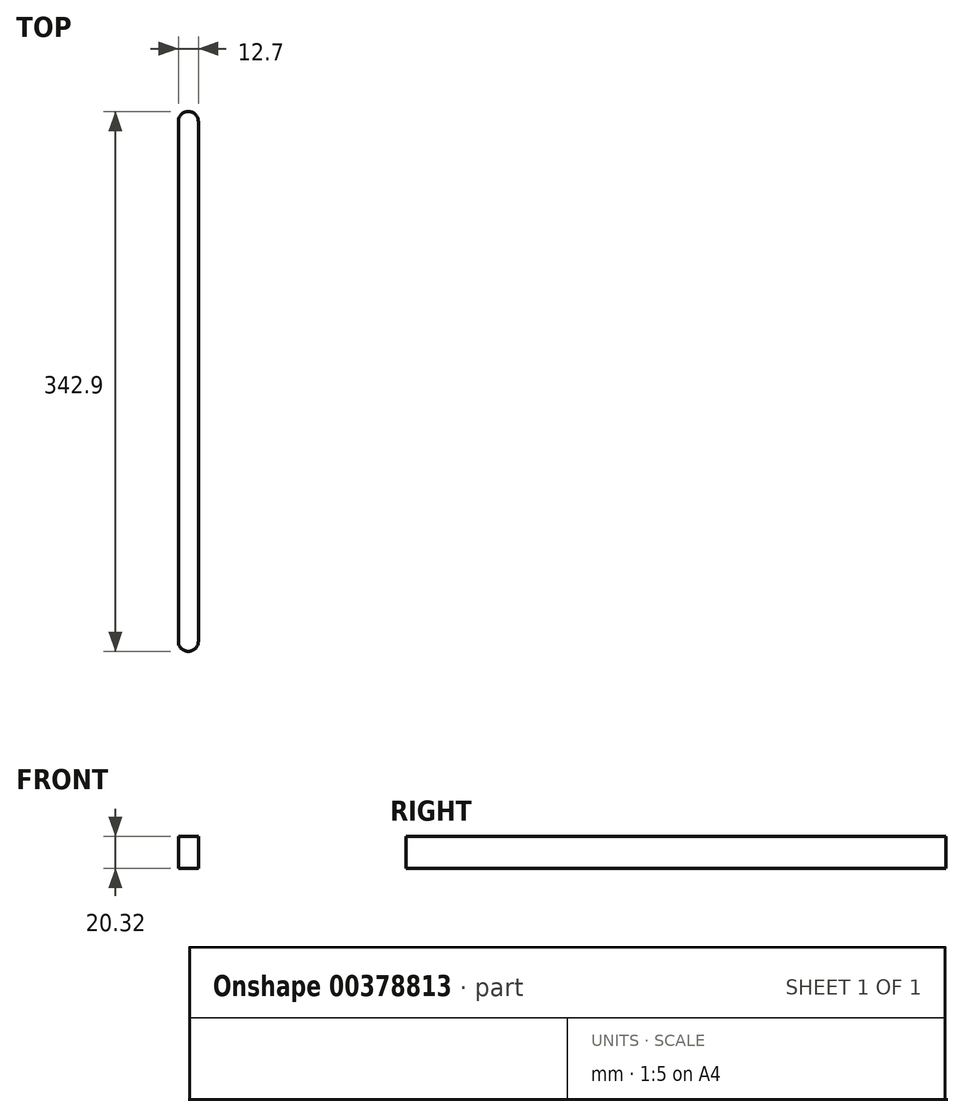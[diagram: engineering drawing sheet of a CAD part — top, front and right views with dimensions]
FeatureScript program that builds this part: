
annotation { "Feature Type Name" : "Feature", "Feature Type Description" : "" }
export const myFeature = defineFeature(function(context is Context, id is Id, definition is map)
    precondition{}
    {
        {
            assignVariable(context, id + "F0", {"name" : "armHeight", "anyValue" : 20.32 * mm});
        }
        {
            var Q0;
            Q0=qCreatedBy(makeId("Top.planeOp"),FACE);
            var sketch = newSketch(context, id + "F1", { "sketchPlane" : qUnion([Q0])});
            skLineSegment(sketch, "E0.bottom", {"start": v(-6.35, 273.3) * mm, "end": v(6.35, 273.3) * mm});
            skLineSegment(sketch, "E0.top", {"start": v(-6.35, -56.9) * mm, "end": v(6.35, -56.9) * mm});
            skLineSegment(sketch, "E0.left", {"start": v(-6.35, 273.3) * mm, "end": v(-6.35, -56.9) * mm});
            skLineSegment(sketch, "E0.right", {"start": v(6.35, 273.3) * mm, "end": v(6.35, -56.9) * mm});
            skCircle(sketch, "E1", {"center": v(0, -56.9) * mm, "radius": 6.35 * mm});
            skCircle(sketch, "E2", {"center": v(0, 273.3) * mm, "radius": 6.35 * mm});
            skSolve(sketch);
        }
        {
            var Q0;
            Q0 = qSketchRegion(id + "F1", true);
            extrude(context, id + "F2", {"entities" : qUnion([Q0]), "depth" : getVariable(context, 'armHeight')});
        }
    });
